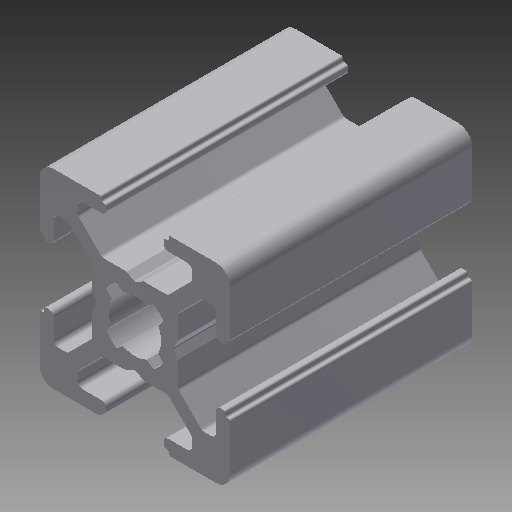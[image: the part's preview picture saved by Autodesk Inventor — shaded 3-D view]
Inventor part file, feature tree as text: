
AUTODESK INVENTOR PART (.ipt)
format: ipt  version: 2019 (Build 230136000, 136)  size: 340,480 bytes
history: native  units: in
note: dims shown in document units (in); Inventor stores cm internally (conversion verified against a paired STEP export)
features: other x3, extrude x1, sketch x1
ambient origin geometry x8: Origin, YZ Plane, XZ Plane, XY Plane, X Axis, Y Axis, Z Axis, Center Point
bodies: Solid1 (feature_tree)
feature tree (5):
  other  "Blocks"
  extrude  "Extrusion1"  Depth=1.0in
  sketch  "Sketch1"  dims[d1=0.0in d13=1.0in d14=1.0in]
  other  "20x20"
  other  "20x20:1"
